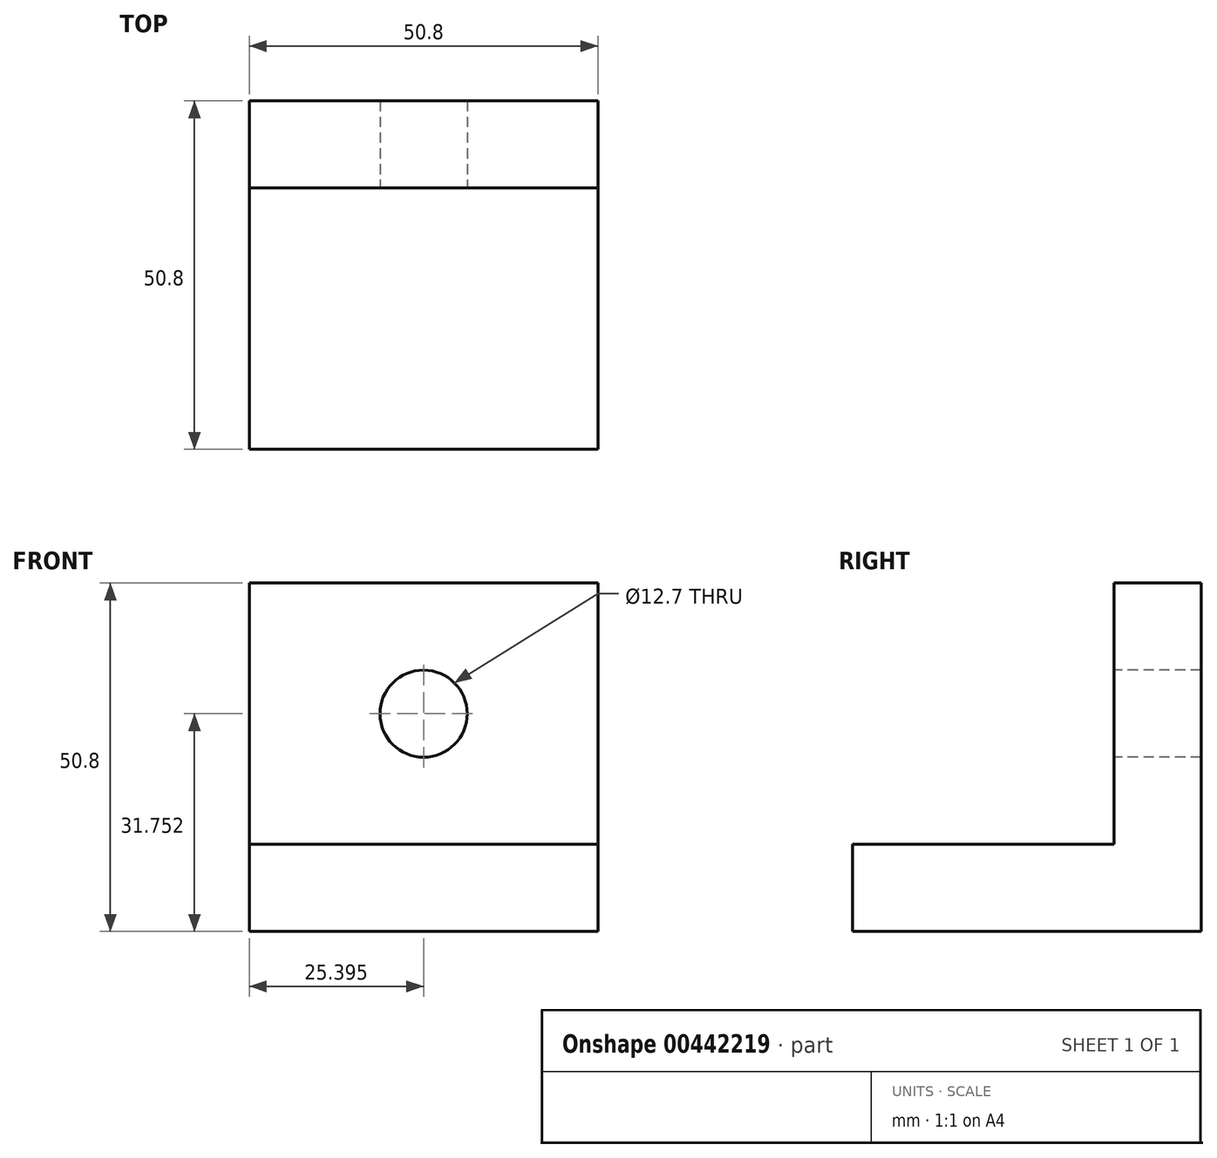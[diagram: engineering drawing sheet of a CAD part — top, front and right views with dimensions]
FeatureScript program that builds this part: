
annotation { "Feature Type Name" : "Feature", "Feature Type Description" : "" }
export const myFeature = defineFeature(function(context is Context, id is Id, definition is map)
    precondition{}
    {
        {
            var Q0;
            Q0=qCreatedBy(makeId("Front.planeOp"),FACE);
            var sketch = newSketch(context, id + "F0", { "sketchPlane" : qUnion([Q0])});
            skLineSegment(sketch, "E0.bottom", {"start": v(-21.97, 24.73) * mm, "end": v(28.83, 24.73) * mm});
            skLineSegment(sketch, "E0.top", {"start": v(-21.97, -26.07) * mm, "end": v(28.83, -26.07) * mm});
            skLineSegment(sketch, "E0.left", {"start": v(-21.97, 24.73) * mm, "end": v(-21.97, -26.07) * mm});
            skLineSegment(sketch, "E0.right", {"start": v(28.83, 24.73) * mm, "end": v(28.83, -26.07) * mm});
            skLineSegment(sketch, "E1", {"start": v(-21.97, -13.37) * mm, "end": v(28.83, -13.37) * mm});
            skSolve(sketch);
        }
        {
            var Q0;
            {var subQ0=sQuery(id+"F0.wireOp",EDGE,"E0.bottom");Q0=makeQuery(id+"F0.imprint","IMPRINT",FACE,{"disambiguationData":[TD([[makeQuery(id+"F0.imprint","IMPRINT",EDGE,{"derivedFrom":subQ0}),-1.0]])]});}
            extrude(context, id + "F1", {"entities" : qUnion([Q0]), "depth" : 12.7 * mm});
        }
        {
            var Q0;
            {var subQ0=sQuery(id+"F0.wireOp",EDGE,"E0.top");Q0=makeQuery(id+"F0.imprint","IMPRINT",FACE,{"disambiguationData":[TD([[makeQuery(id+"F0.imprint","IMPRINT",EDGE,{"derivedFrom":subQ0}),1.0]])]});}
            extrude(context, id + "F2", {"entities" : qUnion([Q0]), "operationType" : NewBodyOperationType.ADD, "depth" : 50.8 * mm});
        }
        {
            var Q0;
            Q0=makeQuery(id+"F1.opExtrude","CAP_FACE",FACE,{"disambiguationData":[OSD([sQuery(id+"F0.wireOp",EDGE,"E0.bottom"),sQuery(id+"F0.wireOp",EDGE,"E0.left"),sQuery(id+"F0.wireOp",EDGE,"E0.right"),sQuery(id+"F0.wireOp",EDGE,"E1")])],"isStart":false});
            var sketch = newSketch(context, id + "F3", { "sketchPlane" : qUnion([Q0])});
            skCircle(sketch, "E2", {"center": v(3.43, 5.68) * mm, "radius": 6.35 * mm});
            skSolve(sketch);
        }
        {
            var Q0;
            Q0=makeQuery(id+"F3.imprint","IMPRINT",FACE,{"disambiguationData":[TD([[makeQuery(id+"F3.imprint","IMPRINT",EDGE,{"derivedFrom":sQuery(id+"F3.wireOp",EDGE,"E2")}),1.0]])]});
            var Q1;
            {var subQ0=sQuery(id+"F0.wireOp",EDGE,"E1");var subQ1=sQuery(id+"F0.wireOp",EDGE,"E0.right");var subQ2=sQuery(id+"F0.wireOp",EDGE,"E0.left");Q1=makeQuery(id+"F2.boolean.opBoolean","MERGE",FACE,{"derivedFrom":[makeQuery(id+"F1.opExtrude","CAP_FACE",FACE,{"disambiguationData":[OSD([sQuery(id+"F0.wireOp",EDGE,"E0.bottom"),subQ2,subQ1,subQ0])],"isStart":true}),makeQuery(id+"F2.opExtrude","CAP_FACE",FACE,{"disambiguationData":[OSD([sQuery(id+"F0.wireOp",EDGE,"E0.top"),subQ2,subQ1,subQ0])],"isStart":true})]});}
            extrude(context, id + "F4", {"entities" : qUnion([Q0]), "operationType" : NewBodyOperationType.REMOVE, "endBound" : BoundingType.UP_TO_SURFACE, "oppositeDirection" : true, "endBoundEntityFace" : qUnion([Q1]), "depth" : 25.4 * mm});
        }
    });
